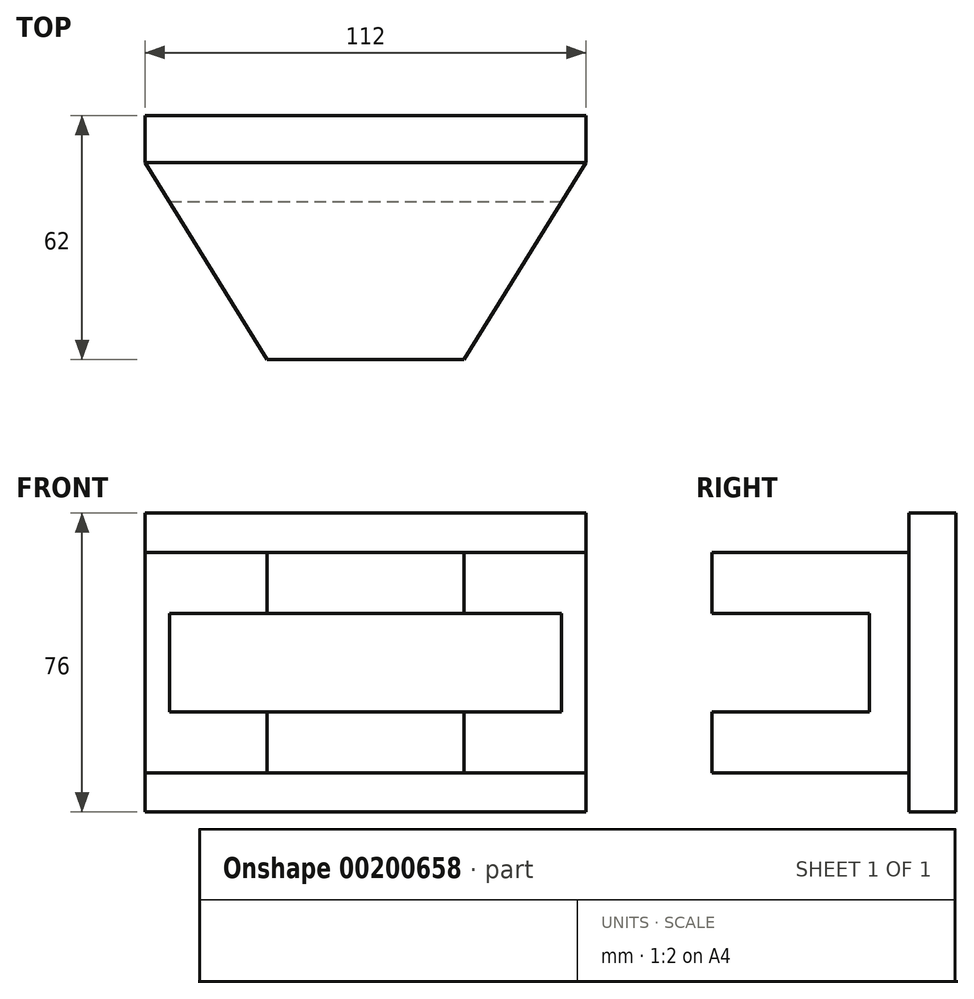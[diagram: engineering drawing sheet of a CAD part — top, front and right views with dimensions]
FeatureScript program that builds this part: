
annotation { "Feature Type Name" : "Feature", "Feature Type Description" : "" }
export const myFeature = defineFeature(function(context is Context, id is Id, definition is map)
    precondition{}
    {
        {
            var Q0;
            Q0=qCreatedBy(makeId("Front.planeOp"),FACE);
            var sketch = newSketch(context, id + "F0", { "sketchPlane" : qUnion([Q0])});
            skLineSegment(sketch, "E0.bottom", {"start": v(-56, 38) * mm, "end": v(56, 38) * mm});
            skLineSegment(sketch, "E0.top", {"start": v(-56, -38) * mm, "end": v(56, -38) * mm});
            skLineSegment(sketch, "E0.left", {"start": v(-56, 38) * mm, "end": v(-56, -38) * mm});
            skLineSegment(sketch, "E0.right", {"start": v(56, 38) * mm, "end": v(56, -38) * mm});
            skSolve(sketch);
        }
        {
            var Q0;
            Q0 = qSketchRegion(id + "F0", true);
            var Q1;
            Q1=makeQuery(id+"F0.imprint","IMPRINT",FACE,{"disambiguationData":[TD([[makeQuery(id+"F0.imprint","IMPRINT",EDGE,{"derivedFrom":sQuery(id+"F0.wireOp",EDGE,"E0.bottom")}),-1.0]])]});
            extrude(context, id + "F1", {"entities" : qUnion([Q0, Q1]), "depth" : 12 * mm});
        }
        {
            var Q0;
            Q0=makeQuery(id+"F1.opExtrude","SWEPT_FACE",FACE,{"disambiguationData":[OSD([sQuery(id+"F0.wireOp",EDGE,"E0.top")])]});
            cPlane(context, id + "F2", {"entities" : qUnion([Q0]), "cplaneType" : CPlaneType.OFFSET, "offset" : 10 * mm, "oppositeDirection" : true, "width" : 150 * mm, "height" : 150 * mm});
        }
        {
            var Q0;
            Q0=qCreatedBy(id+"F2.planeOp",FACE);
            var sketch = newSketch(context, id + "F3", { "sketchPlane" : qUnion([Q0])});
            skLineSegment(sketch, "E1.0", {"start": v(-56, 12) * mm, "end": v(56, 12) * mm});
            skLineSegment(sketch, "E2", {"start": v(-56, 12) * mm, "end": v(-25, 62) * mm});
            skLineSegment(sketch, "E3", {"start": v(-25, 62) * mm, "end": v(25, 62) * mm});
            skLineSegment(sketch, "E4", {"start": v(25, 62) * mm, "end": v(56, 12) * mm});
            skPoint(sketch, "E5.end.orphan", {"position": v(-25, 12) * mm});
            skSolve(sketch);
        }
        {
            var Q0;
            Q0=makeQuery(id+"F3.imprint","IMPRINT",FACE,{"disambiguationData":[TD([[makeQuery(id+"F3.imprint","IMPRINT",EDGE,{"derivedFrom":sQuery(id+"F3.wireOp",EDGE,"E1.0")}),1.0]])]});
            extrude(context, id + "F4", {"entities" : qUnion([Q0]), "operationType" : NewBodyOperationType.ADD, "oppositeDirection" : true, "depth" : 56 * mm});
        }
        {
            var Q0;
            Q0=makeQuery(id+"F4.opExtrude","SWEPT_FACE",FACE,{"disambiguationData":[OSD([sQuery(id+"F3.wireOp",EDGE,"E3")])]});
            var sketch = newSketch(context, id + "F5", { "sketchPlane" : qUnion([Q0])});
            skLineSegment(sketch, "E6.bottom", {"start": v(24.24, -12.5) * mm, "end": v(-33.46, -12.5) * mm});
            skLineSegment(sketch, "E6.top", {"start": v(24.24, 12.5) * mm, "end": v(-33.46, 12.5) * mm});
            skLineSegment(sketch, "E7", {"start": v(24.24, -12.5) * mm, "end": v(71.24, -12.5) * mm});
            skLineSegment(sketch, "E8", {"start": v(71.24, -12.5) * mm, "end": v(71.24, 12.5) * mm});
            skLineSegment(sketch, "E9", {"start": v(71.24, 12.5) * mm, "end": v(24.24, 12.5) * mm});
            skLineSegment(sketch, "E10", {"start": v(-33.46, -12.5) * mm, "end": v(-89.38, -12.5) * mm});
            skLineSegment(sketch, "E11", {"start": v(-89.38, -12.5) * mm, "end": v(-89.38, 12.5) * mm});
            skLineSegment(sketch, "E12", {"start": v(-89.38, 12.5) * mm, "end": v(-33.46, 12.5) * mm});
            skSolve(sketch);
        }
        {
            var Q0;
            {var subQ0=sQuery(id+"F5.wireOp",EDGE,"E10");Q0=makeQuery(id+"F5.imprint","IMPRINT",FACE,{"disambiguationData":[TD([[makeQuery(id+"F5.imprint","IMPRINT",EDGE,{"derivedFrom":subQ0}),-1.0]])]});}
            var Q1;
            {var subQ0=sQuery(id+"F5.wireOp",EDGE,"E8");Q1=makeQuery(id+"F5.imprint","IMPRINT",FACE,{"disambiguationData":[TD([[makeQuery(id+"F5.imprint","IMPRINT",EDGE,{"derivedFrom":subQ0}),1.0]])]});}
            var Q2;
            {var subQ6=sQuery(id+"F5.wireOp",EDGE,"E7");var subQ7=sQuery(id+"F5.wireOp",EDGE,"E6.bottom");var subQ8=makeQuery(id+"F5.imprint","INTERSECT",VERTEX,{"derivedFrom":[subQ7,subQ6]});Q2=makeQuery(id+"F5.imprint","IMPRINT",FACE,{"disambiguationData":[TD([[makeQuery(id+"F5.imprint","IMPRINT",EDGE,{"disambiguationData":[TD([[subQ8,-1.0]])],"derivedFrom":subQ7}),-1.0]])]});}
            extrude(context, id + "F6", {"entities" : qUnion([Q0, Q1, Q2]), "operationType" : NewBodyOperationType.REMOVE, "oppositeDirection" : true, "depth" : 40 * mm});
        }
    });
